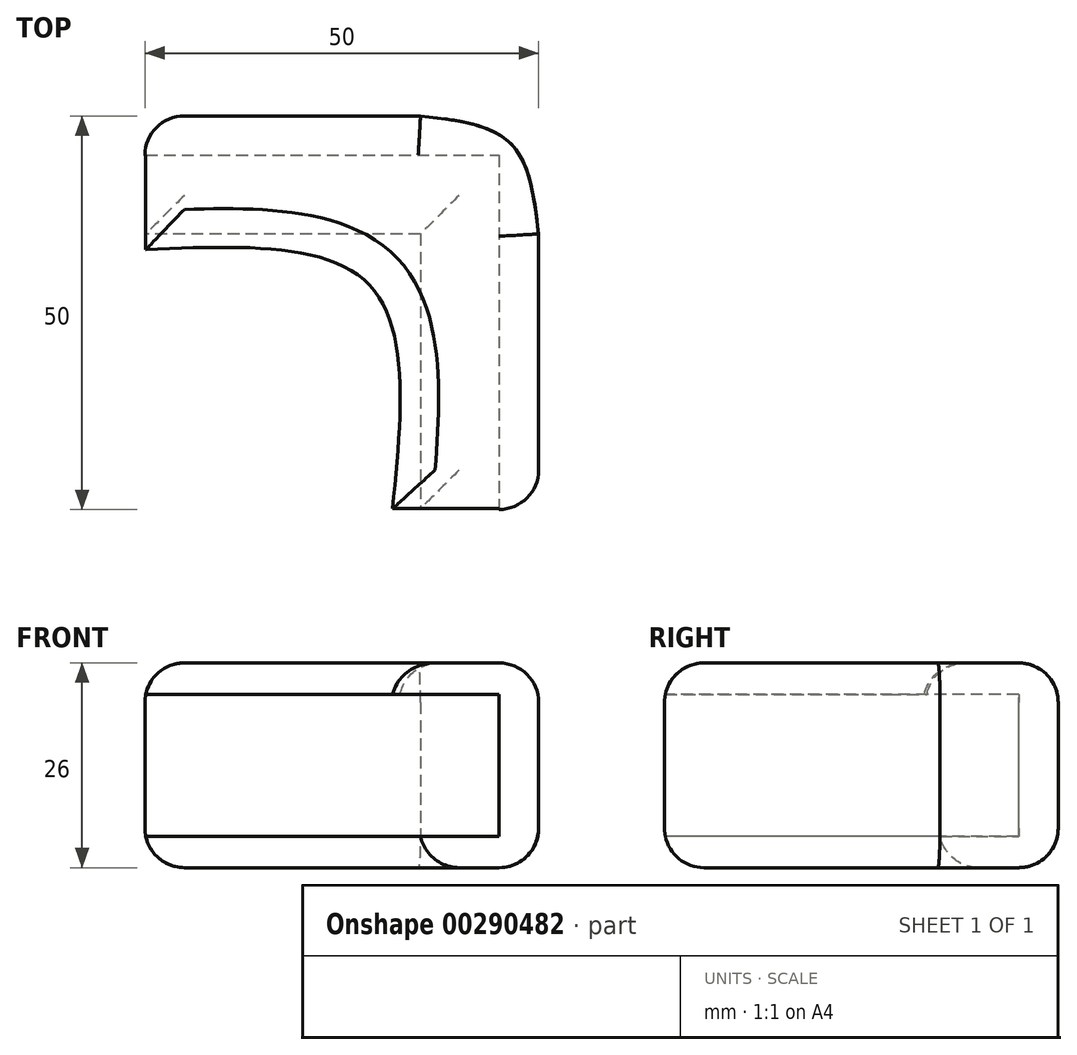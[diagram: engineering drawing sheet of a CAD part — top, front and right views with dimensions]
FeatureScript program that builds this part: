
annotation { "Feature Type Name" : "Feature", "Feature Type Description" : "" }
export const myFeature = defineFeature(function(context is Context, id is Id, definition is map)
    precondition{}
    {
        {
            var Q0;
            Q0=qCreatedBy(makeId("Top.planeOp"),FACE);
            var sketch = newSketch(context, id + "F0", { "sketchPlane" : qUnion([Q0])});
            skLineSegment(sketch, "E0.bottom", {"start": v(40, 40) * mm, "end": v(-40, 40) * mm});
            skLineSegment(sketch, "E0.top", {"start": v(40, -40) * mm, "end": v(-40, -40) * mm});
            skLineSegment(sketch, "E0.left", {"start": v(40, 40) * mm, "end": v(40, -40) * mm});
            skLineSegment(sketch, "E0.right", {"start": v(-40, 40) * mm, "end": v(-40, -40) * mm});
            skPoint(sketch, "E0.middle", {"position": v(0, 0) * mm});
            skLineSegment(sketch, "E1", {"start": v(40, 0) * mm, "end": v(45, 0) * mm});
            skPoint(sketch, "E1.endSnap0", {"position": v(40, 0) * mm});
            skLineSegment(sketch, "E2", {"start": v(0, 40) * mm, "end": v(0, 45) * mm});
            skLineSegment(sketch, "E3", {"start": v(0, 45) * mm, "end": v(45, 45) * mm});
            skLineSegment(sketch, "E4", {"start": v(45, 45) * mm, "end": v(45, 0) * mm});
            skSolve(sketch);
        }
        {
            var Q0;
            Q0 = qSketchRegion(id + "F0", true);
            extrude(context, id + "F1", {"entities" : qUnion([Q0]), "depth" : 18 * mm});
        }
        {
            var Q0;
            Q0=makeQuery(id+"F1.opExtrude","CAP_FACE",FACE,{"disambiguationData":[OSD([sQuery(id+"F0.wireOp",EDGE,"E0.bottom"),sQuery(id+"F0.wireOp",EDGE,"E0.top"),sQuery(id+"F0.wireOp",EDGE,"E0.left"),sQuery(id+"F0.wireOp",EDGE,"E0.right")])],"isStart":false});
            var sketch = newSketch(context, id + "F2", { "sketchPlane" : qUnion([Q0])});
            skLineSegment(sketch, "E5.0", {"start": v(43, 0) * mm, "end": v(43, 43) * mm});
            skLineSegment(sketch, "E5.1", {"start": v(0, 43) * mm, "end": v(43, 43) * mm});
            skLineSegment(sketch, "E6", {"start": v(0, 43) * mm, "end": v(0, 33) * mm});
            skLineSegment(sketch, "E7", {"start": v(43, 0) * mm, "end": v(31.44, 0) * mm});
            skLineSegment(sketch, "E8", {"start": v(43, 43) * mm, "end": v(28.51, 28.51) * mm});
            skFitSpline(sketch, "E9", {"points": [v(31.44, 0) * mm, v(28.51, 28.51) * mm, v(0, 33) * mm], "startDerivative": vector(6.87, 69.15) * mm, "endDerivative": vector(-69.71, -3.1) * mm});
            skLineSegment(sketch, "E10", {"start": v(50, 0) * mm, "end": v(31.44, 0) * mm});
            skLineSegment(sketch, "E11", {"start": v(0, 50) * mm, "end": v(0, 43) * mm});
            skFitSpline(sketch, "E12", {"points": [v(35, 50) * mm, v(46.46, 46.46) * mm, v(50, 35) * mm], "startDerivative": vector(26.9, -3.1) * mm, "endDerivative": vector(3.1, -26.9) * mm});
            skLineSegment(sketch, "E13", {"start": v(0, 50) * mm, "end": v(35, 50) * mm});
            skLineSegment(sketch, "E14", {"start": v(50, 0) * mm, "end": v(50, 35) * mm});
            skSolve(sketch);
        }
        {
            var Q0;
            Q0 = qSketchRegion(id + "F2", true);
            extrude(context, id + "F3", {"entities" : qUnion([Q0]), "operationType" : NewBodyOperationType.ADD, "depth" : 4 * mm});
        }
        {
            var Q0;
            Q0=makeQuery(id+"F3.opExtrude","CAP_FACE",FACE,{"disambiguationData":[OSD([sQuery(id+"F2.wireOp",EDGE,"E6"),sQuery(id+"F2.wireOp",EDGE,"E9"),sQuery(id+"F2.wireOp",EDGE,"E10"),sQuery(id+"F2.wireOp",EDGE,"E11"),sQuery(id+"F2.wireOp",EDGE,"E12"),sQuery(id+"F2.wireOp",EDGE,"E13"),sQuery(id+"F2.wireOp",EDGE,"E14")])],"isStart":true});
            extrude(context, id + "F4", {"entities" : qUnion([Q0]), "operationType" : NewBodyOperationType.ADD, "depth" : 22 * mm});
        }
        {
            var Q0;
            Q0 = qSketchRegion(id + "F0", true);
            extrude(context, id + "F5", {"entities" : qUnion([Q0]), "operationType" : NewBodyOperationType.REMOVE, "depth" : 18 * mm});
        }
        {
            var Q0;
            {var subQ0=sQuery(id+"F0.wireOp",EDGE,"E4");Q0=makeQuery(id+"F5.boolean.opBoolean","MERGE",FACE,{"derivedFrom":[makeQuery(id+"F4.opExtrude","SWEPT_FACE",FACE,{"disambiguationData":[OSD([subQ0])]}),makeQuery(id+"F5.opExtrude","SWEPT_FACE",FACE,{"disambiguationData":[OSD([subQ0])]})]});}
            var sketch = newSketch(context, id + "F6", { "sketchPlane" : qUnion([Q0])});
            skLineSegment(sketch, "E15.bottom", {"start": v(-45, -4) * mm, "end": v(0, -4) * mm});
            skLineSegment(sketch, "E15.top", {"start": v(-45, 0) * mm, "end": v(0, 0) * mm});
            skLineSegment(sketch, "E15.left", {"start": v(-45, -4) * mm, "end": v(-45, 0) * mm});
            skLineSegment(sketch, "E15.right", {"start": v(0, -4) * mm, "end": v(0, 0) * mm});
            skSolve(sketch);
        }
        {
            var Q0;
            Q0 = qSketchRegion(id + "F6", true);
            extrude(context, id + "F7", {"entities" : qUnion([Q0]), "operationType" : NewBodyOperationType.ADD, "depth" : 10 * mm});
        }
        {
            var Q0;
            {var subQ0=sQuery(id+"F0.wireOp",EDGE,"E3");Q0=makeQuery(id+"F5.boolean.opBoolean","MERGE",FACE,{"derivedFrom":[makeQuery(id+"F4.opExtrude","SWEPT_FACE",FACE,{"disambiguationData":[OSD([subQ0])]}),makeQuery(id+"F5.opExtrude","SWEPT_FACE",FACE,{"disambiguationData":[OSD([subQ0])]})]});}
            var sketch = newSketch(context, id + "F8", { "sketchPlane" : qUnion([Q0])});
            skLineSegment(sketch, "E16.bottom", {"start": v(35, -4) * mm, "end": v(0, -4) * mm});
            skLineSegment(sketch, "E16.top", {"start": v(35, 0) * mm, "end": v(0, 0) * mm});
            skLineSegment(sketch, "E16.left", {"start": v(35, -4) * mm, "end": v(35, 0) * mm});
            skLineSegment(sketch, "E16.right", {"start": v(0, -4) * mm, "end": v(0, 0) * mm});
            skSolve(sketch);
        }
        {
            var Q0;
            Q0=makeQuery(id+"F8.imprint","IMPRINT",FACE,{"disambiguationData":[TD([[makeQuery(id+"F8.imprint","IMPRINT",EDGE,{"derivedFrom":sQuery(id+"F8.wireOp",EDGE,"E16.bottom")}),1.0]])]});
            extrude(context, id + "F9", {"entities" : qUnion([Q0]), "operationType" : NewBodyOperationType.ADD, "depth" : 10 * mm});
        }
        {
            var Q0;
            Q0=makeQuery(id+"F3.opExtrude","CAP_FACE",FACE,{"disambiguationData":[OSD([sQuery(id+"F2.wireOp",EDGE,"E6"),sQuery(id+"F2.wireOp",EDGE,"E9"),sQuery(id+"F2.wireOp",EDGE,"E10"),sQuery(id+"F2.wireOp",EDGE,"E11"),sQuery(id+"F2.wireOp",EDGE,"E12"),sQuery(id+"F2.wireOp",EDGE,"E13"),sQuery(id+"F2.wireOp",EDGE,"E14")])],"isStart":false});
            var Q1;
            Q1=makeQuery(id+"F9.boolean.opBoolean","MERGE",FACE,{"derivedFrom":[makeQuery(id+"F7.boolean.opBoolean","MERGE",FACE,{"derivedFrom":[makeQuery(id+"F4.opExtrude","CAP_FACE",FACE,{"disambiguationData":[OSD([sQuery(id+"F2.wireOp",EDGE,"E6"),sQuery(id+"F2.wireOp",EDGE,"E9"),sQuery(id+"F2.wireOp",EDGE,"E10"),sQuery(id+"F2.wireOp",EDGE,"E11"),sQuery(id+"F2.wireOp",EDGE,"E12"),sQuery(id+"F2.wireOp",EDGE,"E13"),sQuery(id+"F2.wireOp",EDGE,"E14")])],"isStart":false}),makeQuery(id+"F7.opExtrude","SWEPT_FACE",FACE,{"disambiguationData":[OSD([sQuery(id+"F6.wireOp",EDGE,"E15.bottom")])]})]}),makeQuery(id+"F9.opExtrude","SWEPT_FACE",FACE,{"disambiguationData":[OSD([sQuery(id+"F8.wireOp",EDGE,"E16.bottom")])]})]});
            var Q2;
            {var subQ0=sQuery(id+"F2.wireOp",EDGE,"E13");var subQ1=sQuery(id+"F2.wireOp",EDGE,"E11");Q2=makeQuery(id+"F4.boolean.opBoolean","MERGE",EDGE,{"derivedFrom":[makeQuery(id+"F3.opExtrude","SWEPT_EDGE",EDGE,{"disambiguationData":[OSD([subQ1,subQ0])]}),makeQuery(id+"F4.opExtrude","SWEPT_EDGE",EDGE,{"disambiguationData":[OSD([subQ1,subQ0])]})]});}
            var Q3;
            {var subQ0=sQuery(id+"F2.wireOp",EDGE,"E14");var subQ1=sQuery(id+"F2.wireOp",EDGE,"E10");Q3=makeQuery(id+"F4.boolean.opBoolean","MERGE",EDGE,{"derivedFrom":[makeQuery(id+"F3.opExtrude","SWEPT_EDGE",EDGE,{"disambiguationData":[OSD([subQ1,subQ0])]}),makeQuery(id+"F4.opExtrude","SWEPT_EDGE",EDGE,{"disambiguationData":[OSD([subQ1,subQ0])]})]});}
            fillet(context, id + "F10", {"entities" : qUnion([Q0, Q1, Q2, Q3]), "radius" : 5 * mm, "tangentPropagation" : true, "allowEdgeOverflow" : false});
        }
    });
